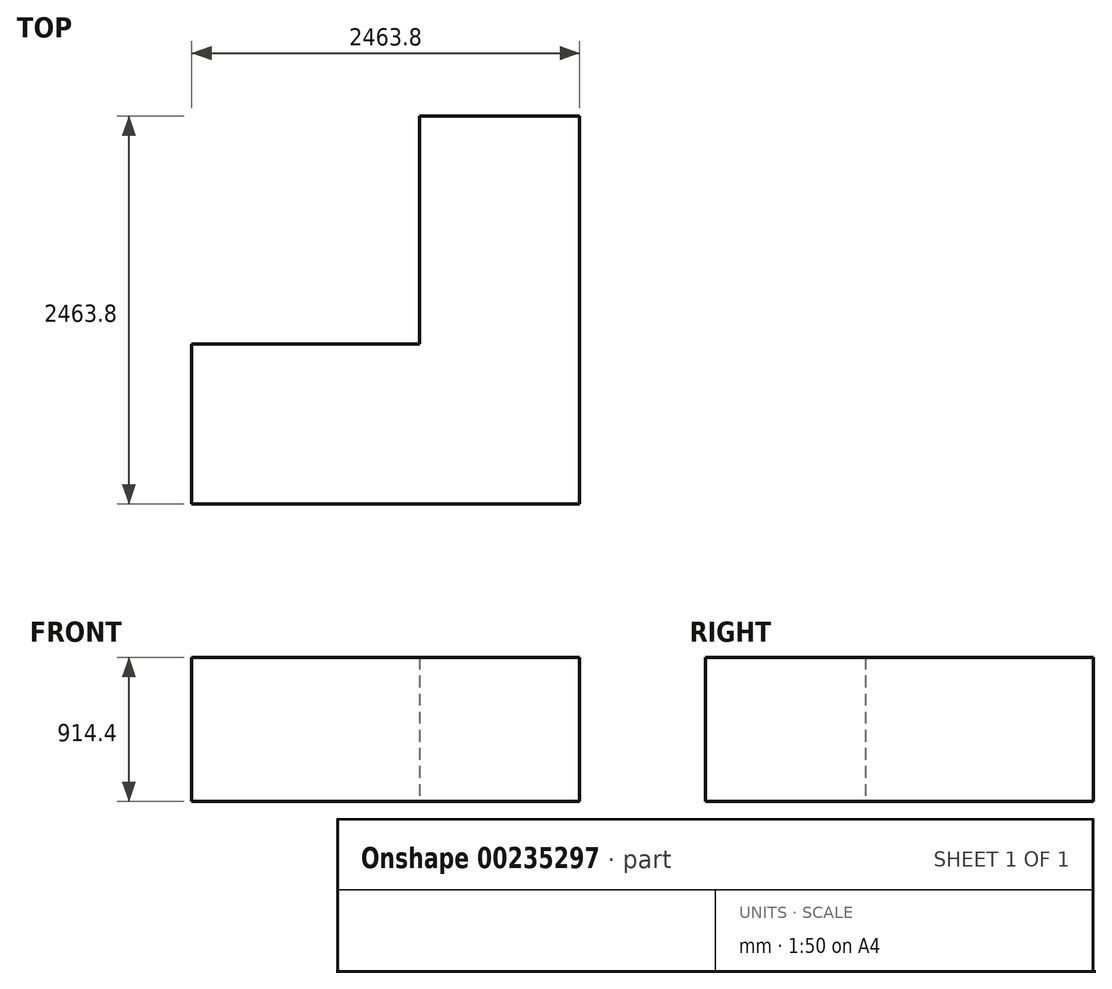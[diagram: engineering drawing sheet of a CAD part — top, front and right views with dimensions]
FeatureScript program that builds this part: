
annotation { "Feature Type Name" : "Feature", "Feature Type Description" : "" }
export const myFeature = defineFeature(function(context is Context, id is Id, definition is map)
    precondition{}
    {
        {
            var Q0;
            Q0=qCreatedBy(makeId("Top.planeOp"),FACE);
            var sketch = newSketch(context, id + "F0", { "sketchPlane" : qUnion([Q0])});
            skLineSegment(sketch, "E0", {"start": v(0, 1447.8) * mm, "end": v(1016, 1447.8) * mm});
            skLineSegment(sketch, "E1", {"start": v(1016, 1447.8) * mm, "end": v(1016, -1016) * mm});
            skLineSegment(sketch, "E2", {"start": v(1016, -1016) * mm, "end": v(-1447.8, -1016) * mm});
            skLineSegment(sketch, "E3", {"start": v(-1447.8, -1016) * mm, "end": v(-1447.8, 0) * mm});
            skLineSegment(sketch, "E4", {"start": v(-1447.8, 0) * mm, "end": v(0, 0) * mm});
            skLineSegment(sketch, "E5", {"start": v(0, 0) * mm, "end": v(0, 1447.8) * mm});
            skSolve(sketch);
        }
        {
            var Q0;
            Q0=makeQuery(id+"F0.imprint","IMPRINT",FACE,{"disambiguationData":[TD([[makeQuery(id+"F0.imprint","IMPRINT",EDGE,{"derivedFrom":sQuery(id+"F0.wireOp",EDGE,"E0")}),-1.0]])]});
            extrude(context, id + "F1", {"entities" : qUnion([Q0]), "depth" : 914.4 * mm});
        }
    });
